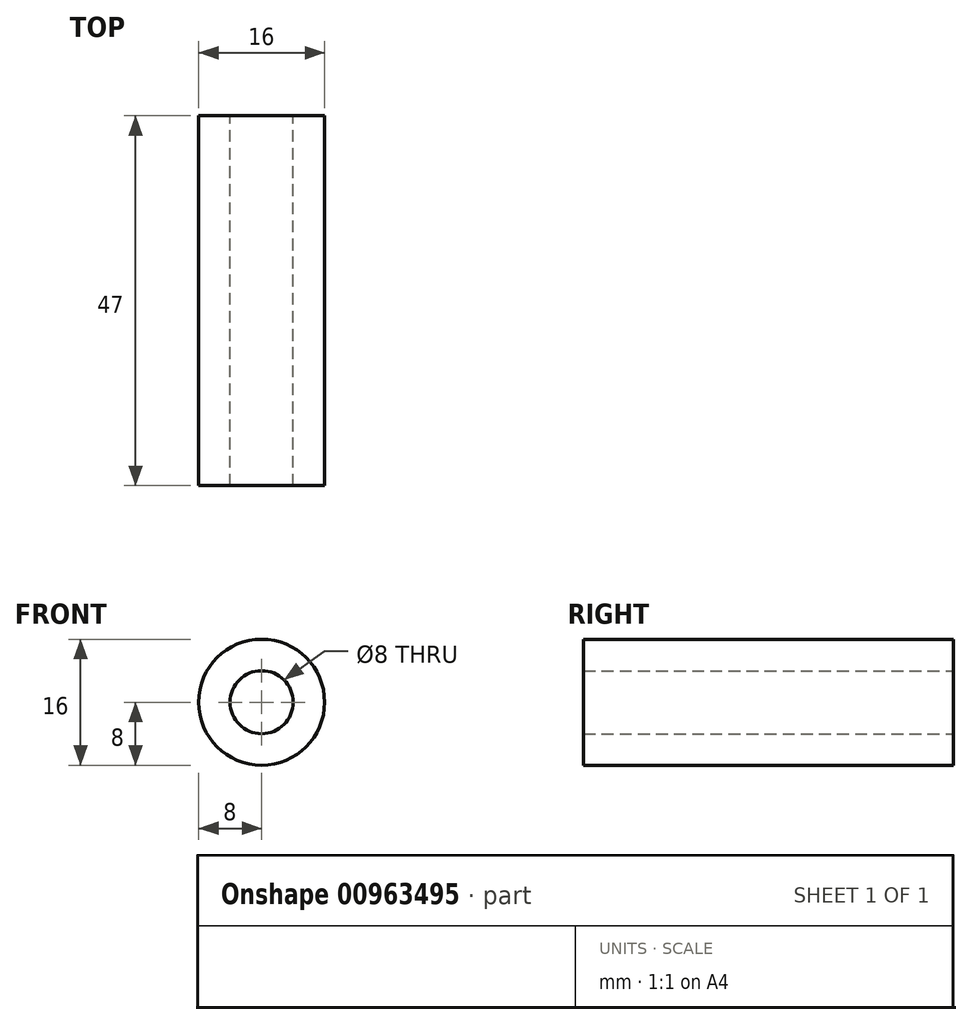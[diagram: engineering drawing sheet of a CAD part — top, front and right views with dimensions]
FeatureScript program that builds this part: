
annotation { "Feature Type Name" : "Feature", "Feature Type Description" : "" }
export const myFeature = defineFeature(function(context is Context, id is Id, definition is map)
    precondition{}
    {
        {
            var Q0;
            Q0=qCreatedBy(makeId("Front.planeOp"),FACE);
            var sketch = newSketch(context, id + "F0", { "sketchPlane" : qUnion([Q0])});
            skCircle(sketch, "E0", {"center": v(0, 0) * mm, "radius": 8 * mm});
            skCircle(sketch, "E1", {"center": v(0, 0) * mm, "radius": 4 * mm});
            skSolve(sketch);
        }
        {
            var Q0;
            Q0=qSketchRegion(id+"F0",true);
            extrude(context, id + "F1", {"entities" : qUnion([Q0]), "depth" : 47 * mm});
        }
    });
